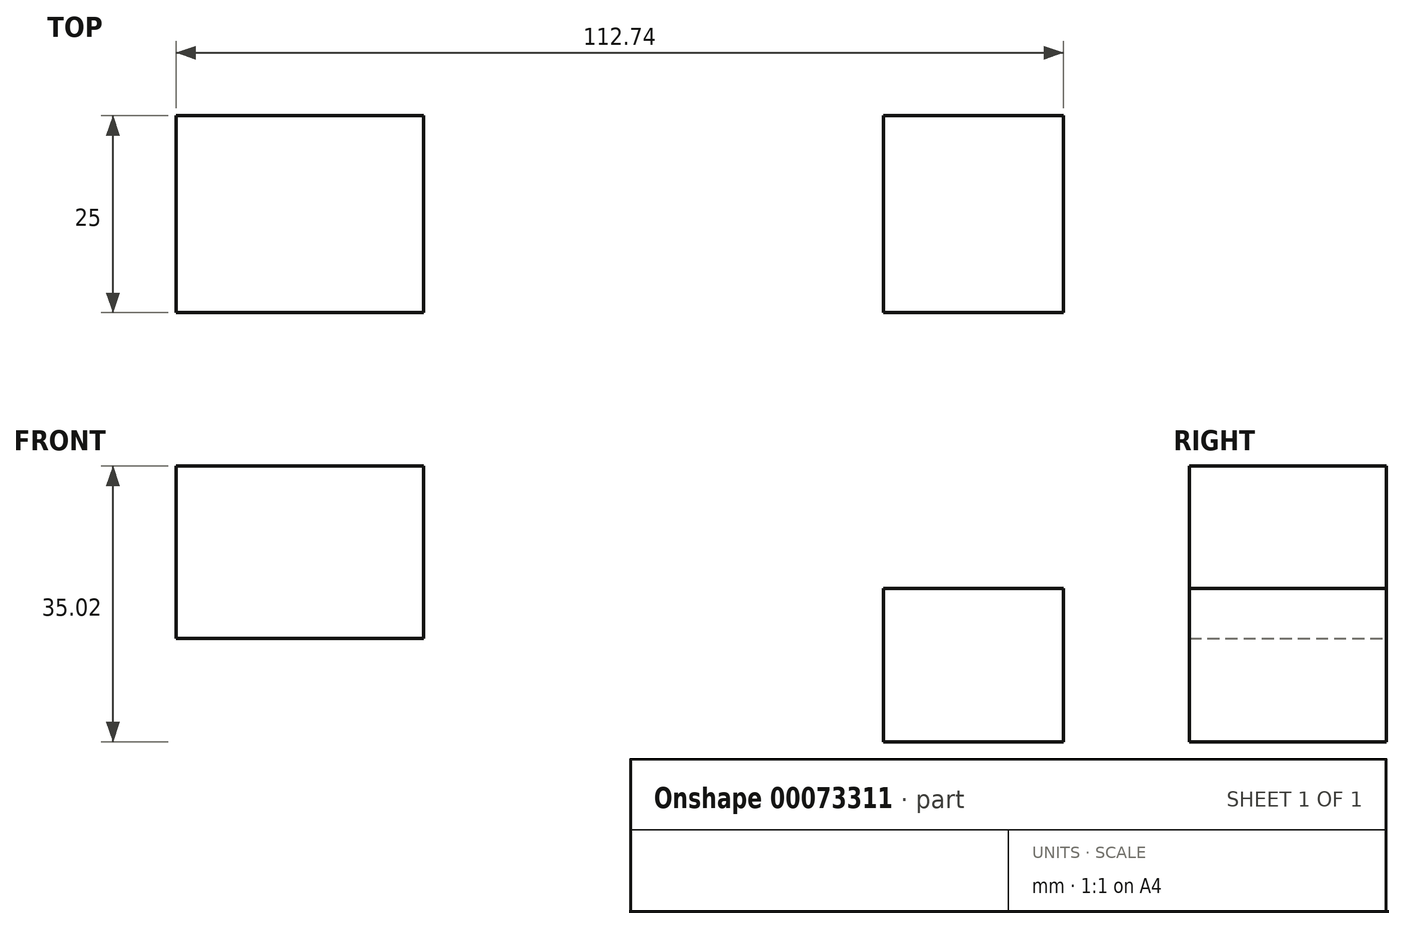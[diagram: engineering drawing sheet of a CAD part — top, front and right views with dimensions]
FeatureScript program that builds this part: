
annotation { "Feature Type Name" : "Feature", "Feature Type Description" : "" }
export const myFeature = defineFeature(function(context is Context, id is Id, definition is map)
    precondition{}
    {
        {
            var Q0;
            Q0=qCreatedBy(makeId("Front.planeOp"),FACE);
            var sketch = newSketch(context, id + "F0", { "sketchPlane" : qUnion([Q0])});
            skLineSegment(sketch, "E0.bottom", {"start": v(-59.7, 49.9) * mm, "end": v(-28.23, 49.9) * mm});
            skLineSegment(sketch, "E0.top", {"start": v(-59.7, 28) * mm, "end": v(-28.23, 28) * mm});
            skLineSegment(sketch, "E0.left", {"start": v(-59.7, 49.9) * mm, "end": v(-59.7, 28) * mm});
            skLineSegment(sketch, "E0.right", {"start": v(-28.23, 49.9) * mm, "end": v(-28.23, 28) * mm});
            skLineSegment(sketch, "E1.bottom", {"start": v(30.2, 14.89) * mm, "end": v(53.04, 14.89) * mm});
            skLineSegment(sketch, "E1.top", {"start": v(30.2, 34.37) * mm, "end": v(53.04, 34.37) * mm});
            skLineSegment(sketch, "E1.left", {"start": v(30.2, 14.89) * mm, "end": v(30.2, 34.37) * mm});
            skLineSegment(sketch, "E1.right", {"start": v(53.04, 14.89) * mm, "end": v(53.04, 34.37) * mm});
            skSolve(sketch);
        }
        {
            var Q0;
            Q0 = qSketchRegion(id + "F0", true);
            extrude(context, id + "F1", {"entities" : qUnion([Q0]), "depth" : 25 * mm});
        }
    });
